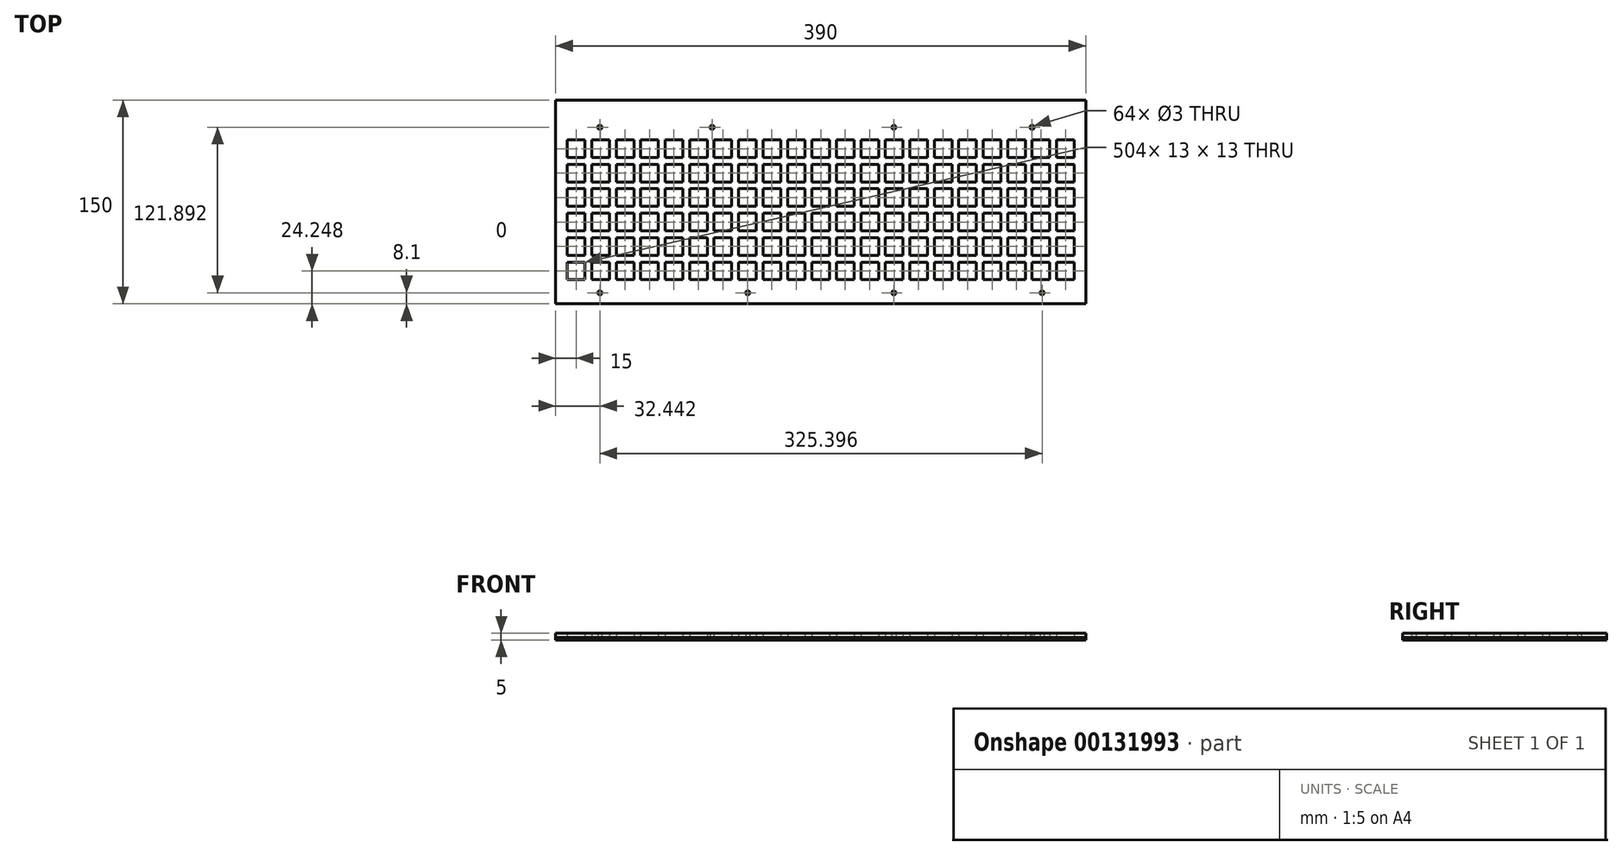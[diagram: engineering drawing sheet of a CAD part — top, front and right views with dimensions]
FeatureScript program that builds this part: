
annotation { "Feature Type Name" : "Feature", "Feature Type Description" : "" }
export const myFeature = defineFeature(function(context is Context, id is Id, definition is map)
    precondition{}
    {
        {
            var Q0;
            Q0=qCreatedBy(makeId("Top.planeOp"),FACE);
            var sketch = newSketch(context, id + "F0", { "sketchPlane" : qUnion([Q0])});
            skLineSegment(sketch, "E0.bottom", {"start": v(0, 0) * mm, "end": v(390, 0) * mm});
            skLineSegment(sketch, "E0.top", {"start": v(0, -150) * mm, "end": v(390, -150) * mm});
            skLineSegment(sketch, "E0.left", {"start": v(0, 0) * mm, "end": v(0, -150) * mm});
            skLineSegment(sketch, "E0.right", {"start": v(390, 0) * mm, "end": v(390, -150) * mm});
            skLineSegment(sketch, "E1.bottom", {"start": v(8.5, -29.25) * mm, "end": v(21.5, -29.25) * mm});
            skLineSegment(sketch, "E1.top", {"start": v(8.5, -42.25) * mm, "end": v(21.5, -42.25) * mm});
            skLineSegment(sketch, "E1.left", {"start": v(8.5, -29.25) * mm, "end": v(8.5, -42.25) * mm});
            skLineSegment(sketch, "E1.right", {"start": v(21.5, -29.25) * mm, "end": v(21.5, -42.25) * mm});
            skLineSegment(sketch, "E2.bottom", {"start": v(8.5, -47.25) * mm, "end": v(21.5, -47.25) * mm});
            skLineSegment(sketch, "E2.top", {"start": v(8.5, -60.25) * mm, "end": v(21.5, -60.25) * mm});
            skLineSegment(sketch, "E2.left", {"start": v(8.5, -47.25) * mm, "end": v(8.5, -60.25) * mm});
            skLineSegment(sketch, "E2.right", {"start": v(21.5, -47.25) * mm, "end": v(21.5, -60.25) * mm});
            skLineSegment(sketch, "E3.bottom", {"start": v(8.5, -65.25) * mm, "end": v(21.5, -65.25) * mm});
            skLineSegment(sketch, "E3.top", {"start": v(8.5, -78.25) * mm, "end": v(21.5, -78.25) * mm});
            skLineSegment(sketch, "E3.left", {"start": v(8.5, -65.25) * mm, "end": v(8.5, -78.25) * mm});
            skLineSegment(sketch, "E3.right", {"start": v(21.5, -65.25) * mm, "end": v(21.5, -78.25) * mm});
            skLineSegment(sketch, "E4.bottom", {"start": v(8.5, -83.25) * mm, "end": v(21.5, -83.25) * mm});
            skLineSegment(sketch, "E4.top", {"start": v(8.5, -96.25) * mm, "end": v(21.5, -96.25) * mm});
            skLineSegment(sketch, "E4.left", {"start": v(8.5, -83.25) * mm, "end": v(8.5, -96.25) * mm});
            skLineSegment(sketch, "E4.right", {"start": v(21.5, -83.25) * mm, "end": v(21.5, -96.25) * mm});
            skLineSegment(sketch, "E5.bottom", {"start": v(8.5, -101.25) * mm, "end": v(21.5, -101.25) * mm});
            skLineSegment(sketch, "E5.top", {"start": v(8.5, -114.25) * mm, "end": v(21.5, -114.25) * mm});
            skLineSegment(sketch, "E5.left", {"start": v(8.5, -101.25) * mm, "end": v(8.5, -114.25) * mm});
            skLineSegment(sketch, "E5.right", {"start": v(21.5, -101.25) * mm, "end": v(21.5, -114.25) * mm});
            skLineSegment(sketch, "E6.bottom", {"start": v(8.5, -119.25) * mm, "end": v(21.5, -119.25) * mm});
            skLineSegment(sketch, "E6.top", {"start": v(8.5, -132.25) * mm, "end": v(21.5, -132.25) * mm});
            skLineSegment(sketch, "E6.left", {"start": v(8.5, -119.25) * mm, "end": v(8.5, -132.25) * mm});
            skLineSegment(sketch, "E6.right", {"start": v(21.5, -119.25) * mm, "end": v(21.5, -132.25) * mm});
            skLineSegment(sketch, "E7", {"start": v(24, -21.56) * mm, "end": v(24, -144.75) * mm, "construction": true});
            skLineSegment(sketch, "E8.MirrorCS", {"start": v(39.5, -47.25) * mm, "end": v(39.5, -60.25) * mm});
            skLineSegment(sketch, "E9.MirrorCS", {"start": v(39.5, -60.25) * mm, "end": v(26.5, -60.25) * mm});
            skLineSegment(sketch, "E10.MirrorCS", {"start": v(39.5, -132.25) * mm, "end": v(26.5, -132.25) * mm});
            skLineSegment(sketch, "E11.MirrorCS", {"start": v(39.5, -119.25) * mm, "end": v(26.5, -119.25) * mm});
            skLineSegment(sketch, "E12.MirrorCS", {"start": v(39.5, -119.25) * mm, "end": v(39.5, -132.25) * mm});
            skLineSegment(sketch, "E13.MirrorCS", {"start": v(26.5, -29.25) * mm, "end": v(26.5, -42.25) * mm});
            skLineSegment(sketch, "E14.MirrorCS", {"start": v(39.5, -29.25) * mm, "end": v(26.5, -29.25) * mm});
            skLineSegment(sketch, "E15.MirrorCS", {"start": v(39.5, -101.25) * mm, "end": v(26.5, -101.25) * mm});
            skLineSegment(sketch, "E16.MirrorCS", {"start": v(26.5, -83.25) * mm, "end": v(26.5, -96.25) * mm});
            skLineSegment(sketch, "E17.MirrorCS", {"start": v(39.5, -83.25) * mm, "end": v(39.5, -96.25) * mm});
            skLineSegment(sketch, "E18.MirrorCS", {"start": v(39.5, -96.25) * mm, "end": v(26.5, -96.25) * mm});
            skLineSegment(sketch, "E19.MirrorCS", {"start": v(39.5, -83.25) * mm, "end": v(26.5, -83.25) * mm});
            skLineSegment(sketch, "E20.MirrorCS", {"start": v(26.5, -65.25) * mm, "end": v(26.5, -78.25) * mm});
            skLineSegment(sketch, "E21.MirrorCS", {"start": v(39.5, -65.25) * mm, "end": v(39.5, -78.25) * mm});
            skLineSegment(sketch, "E22.MirrorCS", {"start": v(39.5, -65.25) * mm, "end": v(26.5, -65.25) * mm});
            skLineSegment(sketch, "E23.MirrorCS", {"start": v(39.5, -78.25) * mm, "end": v(26.5, -78.25) * mm});
            skLineSegment(sketch, "E24.MirrorCS", {"start": v(26.5, -101.25) * mm, "end": v(26.5, -114.25) * mm});
            skLineSegment(sketch, "E25.MirrorCS", {"start": v(26.5, -47.25) * mm, "end": v(26.5, -60.25) * mm});
            skLineSegment(sketch, "E26.MirrorCS", {"start": v(26.5, -119.25) * mm, "end": v(26.5, -132.25) * mm});
            skLineSegment(sketch, "E27.MirrorCS", {"start": v(39.5, -101.25) * mm, "end": v(39.5, -114.25) * mm});
            skLineSegment(sketch, "E28.MirrorCS", {"start": v(39.5, -29.25) * mm, "end": v(39.5, -42.25) * mm});
            skLineSegment(sketch, "E29.MirrorCS", {"start": v(39.5, -114.25) * mm, "end": v(26.5, -114.25) * mm});
            skLineSegment(sketch, "E30.MirrorCS", {"start": v(39.5, -47.25) * mm, "end": v(26.5, -47.25) * mm});
            skLineSegment(sketch, "E31.MirrorCS", {"start": v(39.5, -42.25) * mm, "end": v(26.5, -42.25) * mm});
            skLineSegment(sketch, "E32", {"start": v(42, -21.56) * mm, "end": v(42, -144.75) * mm, "construction": true});
            skLineSegment(sketch, "E33.MirrorCS", {"start": v(57.5, -119.25) * mm, "end": v(57.5, -132.25) * mm});
            skLineSegment(sketch, "E34.MirrorCS", {"start": v(44.5, -29.25) * mm, "end": v(44.5, -42.25) * mm});
            skLineSegment(sketch, "E35.MirrorCS", {"start": v(44.5, -119.25) * mm, "end": v(44.5, -132.25) * mm});
            skLineSegment(sketch, "E36.MirrorCS", {"start": v(44.5, -114.25) * mm, "end": v(57.5, -114.25) * mm});
            skLineSegment(sketch, "E37.MirrorCS", {"start": v(75.5, -83.25) * mm, "end": v(75.5, -96.25) * mm});
            skLineSegment(sketch, "E38.MirrorCS", {"start": v(62.5, -65.25) * mm, "end": v(62.5, -78.25) * mm});
            skLineSegment(sketch, "E39.MirrorCS", {"start": v(75.5, -114.25) * mm, "end": v(62.5, -114.25) * mm});
            skLineSegment(sketch, "E40.MirrorCS", {"start": v(75.5, -42.25) * mm, "end": v(62.5, -42.25) * mm});
            skLineSegment(sketch, "E41.MirrorCS", {"start": v(57.5, -83.25) * mm, "end": v(57.5, -96.25) * mm});
            skLineSegment(sketch, "E42.MirrorCS", {"start": v(75.5, -101.25) * mm, "end": v(75.5, -114.25) * mm});
            skLineSegment(sketch, "E43.MirrorCS", {"start": v(75.5, -29.25) * mm, "end": v(75.5, -42.25) * mm});
            skLineSegment(sketch, "E44.MirrorCS", {"start": v(44.5, -83.25) * mm, "end": v(44.5, -96.25) * mm});
            skLineSegment(sketch, "E45.MirrorCS", {"start": v(44.5, -96.25) * mm, "end": v(57.5, -96.25) * mm});
            skLineSegment(sketch, "E46.MirrorCS", {"start": v(62.5, -101.25) * mm, "end": v(62.5, -114.25) * mm});
            skLineSegment(sketch, "E47.MirrorCS", {"start": v(62.5, -29.25) * mm, "end": v(62.5, -42.25) * mm});
            skLineSegment(sketch, "E48.MirrorCS", {"start": v(44.5, -83.25) * mm, "end": v(57.5, -83.25) * mm});
            skLineSegment(sketch, "E49.MirrorCS", {"start": v(75.5, -119.25) * mm, "end": v(62.5, -119.25) * mm});
            skLineSegment(sketch, "E50.MirrorCS", {"start": v(75.5, -47.25) * mm, "end": v(62.5, -47.25) * mm});
            skLineSegment(sketch, "E51.MirrorCS", {"start": v(57.5, -65.25) * mm, "end": v(57.5, -78.25) * mm});
            skLineSegment(sketch, "E52.MirrorCS", {"start": v(75.5, -60.25) * mm, "end": v(62.5, -60.25) * mm});
            skLineSegment(sketch, "E53.MirrorCS", {"start": v(75.5, -132.25) * mm, "end": v(62.5, -132.25) * mm});
            skLineSegment(sketch, "E54.MirrorCS", {"start": v(44.5, -132.25) * mm, "end": v(57.5, -132.25) * mm});
            skLineSegment(sketch, "E55.MirrorCS", {"start": v(75.5, -78.25) * mm, "end": v(62.5, -78.25) * mm});
            skLineSegment(sketch, "E56.MirrorCS", {"start": v(57.5, -101.25) * mm, "end": v(57.5, -114.25) * mm});
            skLineSegment(sketch, "E57.MirrorCS", {"start": v(44.5, -47.25) * mm, "end": v(44.5, -60.25) * mm});
            skLineSegment(sketch, "E58.MirrorCS", {"start": v(44.5, -65.25) * mm, "end": v(44.5, -78.25) * mm});
            skLineSegment(sketch, "E59.MirrorCS", {"start": v(75.5, -119.25) * mm, "end": v(75.5, -132.25) * mm});
            skLineSegment(sketch, "E60.MirrorCS", {"start": v(75.5, -47.25) * mm, "end": v(75.5, -60.25) * mm});
            skLineSegment(sketch, "E61.MirrorCS", {"start": v(75.5, -65.25) * mm, "end": v(75.5, -78.25) * mm});
            skLineSegment(sketch, "E62.MirrorCS", {"start": v(57.5, -47.25) * mm, "end": v(57.5, -60.25) * mm});
            skLineSegment(sketch, "E63.MirrorCS", {"start": v(44.5, -60.25) * mm, "end": v(57.5, -60.25) * mm});
            skLineSegment(sketch, "E64.MirrorCS", {"start": v(44.5, -65.25) * mm, "end": v(57.5, -65.25) * mm});
            skLineSegment(sketch, "E65.MirrorCS", {"start": v(62.5, -119.25) * mm, "end": v(62.5, -132.25) * mm});
            skLineSegment(sketch, "E66.MirrorCS", {"start": v(62.5, -47.25) * mm, "end": v(62.5, -60.25) * mm});
            skLineSegment(sketch, "E67.MirrorCS", {"start": v(44.5, -119.25) * mm, "end": v(57.5, -119.25) * mm});
            skLineSegment(sketch, "E68.MirrorCS", {"start": v(44.5, -101.25) * mm, "end": v(44.5, -114.25) * mm});
            skLineSegment(sketch, "E69.MirrorCS", {"start": v(75.5, -83.25) * mm, "end": v(62.5, -83.25) * mm});
            skLineSegment(sketch, "E70.MirrorCS", {"start": v(44.5, -101.25) * mm, "end": v(57.5, -101.25) * mm});
            skLineSegment(sketch, "E71.MirrorCS", {"start": v(75.5, -96.25) * mm, "end": v(62.5, -96.25) * mm});
            skLineSegment(sketch, "E72.MirrorCS", {"start": v(44.5, -78.25) * mm, "end": v(57.5, -78.25) * mm});
            skLineSegment(sketch, "E73.MirrorCS", {"start": v(75.5, -65.25) * mm, "end": v(62.5, -65.25) * mm});
            skLineSegment(sketch, "E74.MirrorCS", {"start": v(44.5, -42.25) * mm, "end": v(57.5, -42.25) * mm});
            skLineSegment(sketch, "E75.MirrorCS", {"start": v(44.5, -47.25) * mm, "end": v(57.5, -47.25) * mm});
            skLineSegment(sketch, "E76.MirrorCS", {"start": v(62.5, -83.25) * mm, "end": v(62.5, -96.25) * mm});
            skLineSegment(sketch, "E77.MirrorCS", {"start": v(75.5, -29.25) * mm, "end": v(62.5, -29.25) * mm});
            skLineSegment(sketch, "E78.MirrorCS", {"start": v(44.5, -29.25) * mm, "end": v(57.5, -29.25) * mm});
            skLineSegment(sketch, "E79.MirrorCS", {"start": v(75.5, -101.25) * mm, "end": v(62.5, -101.25) * mm});
            skLineSegment(sketch, "E80.MirrorCS", {"start": v(57.5, -29.25) * mm, "end": v(57.5, -42.25) * mm});
            skLineSegment(sketch, "E81", {"start": v(78, -21.56) * mm, "end": v(78, -144.75) * mm, "construction": true});
            skLineSegment(sketch, "E82.MirrorCS", {"start": v(111.5, -29.25) * mm, "end": v(111.5, -42.25) * mm});
            skLineSegment(sketch, "E83.MirrorCS", {"start": v(116.5, -83.25) * mm, "end": v(116.5, -96.25) * mm});
            skLineSegment(sketch, "E84.MirrorCS", {"start": v(93.5, -119.25) * mm, "end": v(93.5, -132.25) * mm});
            skLineSegment(sketch, "E85.MirrorCS", {"start": v(147.5, -47.25) * mm, "end": v(134.5, -47.25) * mm});
            skLineSegment(sketch, "E86.MirrorCS", {"start": v(147.5, -101.25) * mm, "end": v(134.5, -101.25) * mm});
            skLineSegment(sketch, "E87.MirrorCS", {"start": v(147.5, -29.25) * mm, "end": v(134.5, -29.25) * mm});
            skLineSegment(sketch, "E88.MirrorCS", {"start": v(147.5, -119.25) * mm, "end": v(134.5, -119.25) * mm});
            skLineSegment(sketch, "E89.MirrorCS", {"start": v(116.5, -83.25) * mm, "end": v(129.5, -83.25) * mm});
            skLineSegment(sketch, "E90.MirrorCS", {"start": v(111.5, -119.25) * mm, "end": v(111.5, -132.25) * mm});
            skLineSegment(sketch, "E91.MirrorCS", {"start": v(98.5, -29.25) * mm, "end": v(98.5, -42.25) * mm});
            skLineSegment(sketch, "E92.MirrorCS", {"start": v(129.5, -83.25) * mm, "end": v(129.5, -96.25) * mm});
            skLineSegment(sketch, "E93.MirrorCS", {"start": v(147.5, -65.25) * mm, "end": v(147.5, -78.25) * mm});
            skLineSegment(sketch, "E94.MirrorCS", {"start": v(116.5, -29.25) * mm, "end": v(129.5, -29.25) * mm});
            skLineSegment(sketch, "E95.MirrorCS", {"start": v(116.5, -47.25) * mm, "end": v(129.5, -47.25) * mm});
            skLineSegment(sketch, "E96.MirrorCS", {"start": v(93.5, -101.25) * mm, "end": v(93.5, -114.25) * mm});
            skLineSegment(sketch, "E97.MirrorCS", {"start": v(98.5, -47.25) * mm, "end": v(98.5, -60.25) * mm});
            skLineSegment(sketch, "E98.MirrorCS", {"start": v(93.5, -47.25) * mm, "end": v(93.5, -60.25) * mm});
            skLineSegment(sketch, "E99.MirrorCS", {"start": v(134.5, -83.25) * mm, "end": v(134.5, -96.25) * mm});
            skLineSegment(sketch, "E100.MirrorCS", {"start": v(111.5, -29.25) * mm, "end": v(98.5, -29.25) * mm});
            skLineSegment(sketch, "E101.MirrorCS", {"start": v(80.5, -29.25) * mm, "end": v(93.5, -29.25) * mm});
            skLineSegment(sketch, "E102.MirrorCS", {"start": v(129.5, -29.25) * mm, "end": v(129.5, -42.25) * mm});
            skLineSegment(sketch, "E103.MirrorCS", {"start": v(116.5, -114.25) * mm, "end": v(129.5, -114.25) * mm});
            skLineSegment(sketch, "E104.MirrorCS", {"start": v(111.5, -96.25) * mm, "end": v(98.5, -96.25) * mm});
            skLineSegment(sketch, "E105.MirrorCS", {"start": v(80.5, -65.25) * mm, "end": v(80.5, -78.25) * mm});
            skLineSegment(sketch, "E106.MirrorCS", {"start": v(93.5, -83.25) * mm, "end": v(93.5, -96.25) * mm});
            skLineSegment(sketch, "E107.MirrorCS", {"start": v(116.5, -119.25) * mm, "end": v(116.5, -132.25) * mm});
            skLineSegment(sketch, "E108.MirrorCS", {"start": v(116.5, -29.25) * mm, "end": v(116.5, -42.25) * mm});
            skLineSegment(sketch, "E109.MirrorCS", {"start": v(111.5, -83.25) * mm, "end": v(111.5, -96.25) * mm});
            skLineSegment(sketch, "E110.MirrorCS", {"start": v(80.5, -47.25) * mm, "end": v(80.5, -60.25) * mm});
            skLineSegment(sketch, "E111.MirrorCS", {"start": v(147.5, -96.25) * mm, "end": v(134.5, -96.25) * mm});
            skLineSegment(sketch, "E112.MirrorCS", {"start": v(134.5, -29.25) * mm, "end": v(134.5, -42.25) * mm});
            skLineSegment(sketch, "E113.MirrorCS", {"start": v(80.5, -132.25) * mm, "end": v(93.5, -132.25) * mm});
            skLineSegment(sketch, "E114.MirrorCS", {"start": v(80.5, -83.25) * mm, "end": v(93.5, -83.25) * mm});
            skLineSegment(sketch, "E115.MirrorCS", {"start": v(147.5, -47.25) * mm, "end": v(147.5, -60.25) * mm});
            skLineSegment(sketch, "E116.MirrorCS", {"start": v(147.5, -119.25) * mm, "end": v(147.5, -132.25) * mm});
            skLineSegment(sketch, "E117.MirrorCS", {"start": v(116.5, -65.25) * mm, "end": v(116.5, -78.25) * mm});
            skLineSegment(sketch, "E118.MirrorCS", {"start": v(80.5, -83.25) * mm, "end": v(80.5, -96.25) * mm});
            skLineSegment(sketch, "E119.MirrorCS", {"start": v(134.5, -101.25) * mm, "end": v(134.5, -114.25) * mm});
            skLineSegment(sketch, "E120.MirrorCS", {"start": v(111.5, -47.25) * mm, "end": v(98.5, -47.25) * mm});
            skLineSegment(sketch, "E121.MirrorCS", {"start": v(116.5, -101.25) * mm, "end": v(116.5, -114.25) * mm});
            skLineSegment(sketch, "E122.MirrorCS", {"start": v(116.5, -119.25) * mm, "end": v(129.5, -119.25) * mm});
            skLineSegment(sketch, "E123.MirrorCS", {"start": v(80.5, -29.25) * mm, "end": v(80.5, -42.25) * mm});
            skLineSegment(sketch, "E124.MirrorCS", {"start": v(80.5, -119.25) * mm, "end": v(80.5, -132.25) * mm});
            skLineSegment(sketch, "E125.MirrorCS", {"start": v(147.5, -83.25) * mm, "end": v(134.5, -83.25) * mm});
            skLineSegment(sketch, "E126.MirrorCS", {"start": v(111.5, -42.25) * mm, "end": v(98.5, -42.25) * mm});
            skLineSegment(sketch, "E127.MirrorCS", {"start": v(116.5, -132.25) * mm, "end": v(129.5, -132.25) * mm});
            skLineSegment(sketch, "E128.MirrorCS", {"start": v(129.5, -119.25) * mm, "end": v(129.5, -132.25) * mm});
            skLineSegment(sketch, "E129.MirrorCS", {"start": v(80.5, -101.25) * mm, "end": v(80.5, -114.25) * mm});
            skLineSegment(sketch, "E130.MirrorCS", {"start": v(111.5, -65.25) * mm, "end": v(111.5, -78.25) * mm});
            skLineSegment(sketch, "E131.MirrorCS", {"start": v(80.5, -60.25) * mm, "end": v(93.5, -60.25) * mm});
            skLineSegment(sketch, "E132.MirrorCS", {"start": v(111.5, -101.25) * mm, "end": v(111.5, -114.25) * mm});
            skLineSegment(sketch, "E133.MirrorCS", {"start": v(134.5, -65.25) * mm, "end": v(134.5, -78.25) * mm});
            skLineSegment(sketch, "E134.MirrorCS", {"start": v(147.5, -60.25) * mm, "end": v(134.5, -60.25) * mm});
            skLineSegment(sketch, "E135.MirrorCS", {"start": v(147.5, -132.25) * mm, "end": v(134.5, -132.25) * mm});
            skLineSegment(sketch, "E136.MirrorCS", {"start": v(129.5, -65.25) * mm, "end": v(129.5, -78.25) * mm});
            skLineSegment(sketch, "E137.MirrorCS", {"start": v(111.5, -114.25) * mm, "end": v(98.5, -114.25) * mm});
            skLineSegment(sketch, "E138.MirrorCS", {"start": v(80.5, -65.25) * mm, "end": v(93.5, -65.25) * mm});
            skLineSegment(sketch, "E139.MirrorCS", {"start": v(116.5, -60.25) * mm, "end": v(129.5, -60.25) * mm});
            skLineSegment(sketch, "E140.MirrorCS", {"start": v(129.5, -47.25) * mm, "end": v(129.5, -60.25) * mm});
            skLineSegment(sketch, "E141.MirrorCS", {"start": v(98.5, -83.25) * mm, "end": v(98.5, -96.25) * mm});
            skLineSegment(sketch, "E142.MirrorCS", {"start": v(111.5, -47.25) * mm, "end": v(111.5, -60.25) * mm});
            skLineSegment(sketch, "E143.MirrorCS", {"start": v(80.5, -47.25) * mm, "end": v(93.5, -47.25) * mm});
            skLineSegment(sketch, "E144.MirrorCS", {"start": v(116.5, -96.25) * mm, "end": v(129.5, -96.25) * mm});
            skLineSegment(sketch, "E145.MirrorCS", {"start": v(111.5, -119.25) * mm, "end": v(98.5, -119.25) * mm});
            skLineSegment(sketch, "E146.MirrorCS", {"start": v(98.5, -65.25) * mm, "end": v(98.5, -78.25) * mm});
            skLineSegment(sketch, "E147.MirrorCS", {"start": v(111.5, -60.25) * mm, "end": v(98.5, -60.25) * mm});
            skLineSegment(sketch, "E148.MirrorCS", {"start": v(147.5, -83.25) * mm, "end": v(147.5, -96.25) * mm});
            skLineSegment(sketch, "E149.MirrorCS", {"start": v(111.5, -65.25) * mm, "end": v(98.5, -65.25) * mm});
            skLineSegment(sketch, "E150.MirrorCS", {"start": v(111.5, -83.25) * mm, "end": v(98.5, -83.25) * mm});
            skLineSegment(sketch, "E151.MirrorCS", {"start": v(116.5, -42.25) * mm, "end": v(129.5, -42.25) * mm});
            skLineSegment(sketch, "E152.MirrorCS", {"start": v(147.5, -42.25) * mm, "end": v(134.5, -42.25) * mm});
            skLineSegment(sketch, "E153.MirrorCS", {"start": v(147.5, -114.25) * mm, "end": v(134.5, -114.25) * mm});
            skLineSegment(sketch, "E154.MirrorCS", {"start": v(98.5, -101.25) * mm, "end": v(98.5, -114.25) * mm});
            skLineSegment(sketch, "E155.MirrorCS", {"start": v(80.5, -42.25) * mm, "end": v(93.5, -42.25) * mm});
            skLineSegment(sketch, "E156.MirrorCS", {"start": v(129.5, -101.25) * mm, "end": v(129.5, -114.25) * mm});
            skLineSegment(sketch, "E157.MirrorCS", {"start": v(116.5, -47.25) * mm, "end": v(116.5, -60.25) * mm});
            skLineSegment(sketch, "E158.MirrorCS", {"start": v(111.5, -78.25) * mm, "end": v(98.5, -78.25) * mm});
            skLineSegment(sketch, "E159.MirrorCS", {"start": v(147.5, -101.25) * mm, "end": v(147.5, -114.25) * mm});
            skLineSegment(sketch, "E160.MirrorCS", {"start": v(93.5, -29.25) * mm, "end": v(93.5, -42.25) * mm});
            skLineSegment(sketch, "E161.MirrorCS", {"start": v(116.5, -101.25) * mm, "end": v(129.5, -101.25) * mm});
            skLineSegment(sketch, "E162.MirrorCS", {"start": v(80.5, -101.25) * mm, "end": v(93.5, -101.25) * mm});
            skLineSegment(sketch, "E163.MirrorCS", {"start": v(147.5, -29.25) * mm, "end": v(147.5, -42.25) * mm});
            skLineSegment(sketch, "E164.MirrorCS", {"start": v(80.5, -119.25) * mm, "end": v(93.5, -119.25) * mm});
            skLineSegment(sketch, "E165.MirrorCS", {"start": v(98.5, -119.25) * mm, "end": v(98.5, -132.25) * mm});
            skLineSegment(sketch, "E166.MirrorCS", {"start": v(147.5, -78.25) * mm, "end": v(134.5, -78.25) * mm});
            skLineSegment(sketch, "E167.MirrorCS", {"start": v(147.5, -65.25) * mm, "end": v(134.5, -65.25) * mm});
            skLineSegment(sketch, "E168.MirrorCS", {"start": v(80.5, -78.25) * mm, "end": v(93.5, -78.25) * mm});
            skLineSegment(sketch, "E169.MirrorCS", {"start": v(80.5, -96.25) * mm, "end": v(93.5, -96.25) * mm});
            skLineSegment(sketch, "E170.MirrorCS", {"start": v(116.5, -78.25) * mm, "end": v(129.5, -78.25) * mm});
            skLineSegment(sketch, "E171.MirrorCS", {"start": v(80.5, -114.25) * mm, "end": v(93.5, -114.25) * mm});
            skLineSegment(sketch, "E172.MirrorCS", {"start": v(134.5, -119.25) * mm, "end": v(134.5, -132.25) * mm});
            skLineSegment(sketch, "E173.MirrorCS", {"start": v(116.5, -65.25) * mm, "end": v(129.5, -65.25) * mm});
            skLineSegment(sketch, "E174.MirrorCS", {"start": v(93.5, -65.25) * mm, "end": v(93.5, -78.25) * mm});
            skLineSegment(sketch, "E175.MirrorCS", {"start": v(134.5, -47.25) * mm, "end": v(134.5, -60.25) * mm});
            skLineSegment(sketch, "E176.MirrorCS", {"start": v(111.5, -101.25) * mm, "end": v(98.5, -101.25) * mm});
            skLineSegment(sketch, "E177.MirrorCS", {"start": v(111.5, -132.25) * mm, "end": v(98.5, -132.25) * mm});
            skLineSegment(sketch, "E178", {"start": v(150, -21.56) * mm, "end": v(150, -144.75) * mm, "construction": true});
            skLineSegment(sketch, "E179.MirrorCS", {"start": v(291.5, -83.25) * mm, "end": v(291.5, -96.25) * mm});
            skLineSegment(sketch, "E180.MirrorCS", {"start": v(291.5, -101.25) * mm, "end": v(278.5, -101.25) * mm});
            skLineSegment(sketch, "E181.MirrorCS", {"start": v(291.5, -29.25) * mm, "end": v(278.5, -29.25) * mm});
            skLineSegment(sketch, "E182.MirrorCS", {"start": v(291.5, -29.25) * mm, "end": v(291.5, -42.25) * mm});
            skLineSegment(sketch, "E183.MirrorCS", {"start": v(291.5, -47.25) * mm, "end": v(291.5, -60.25) * mm});
            skLineSegment(sketch, "E184.MirrorCS", {"start": v(291.5, -119.25) * mm, "end": v(291.5, -132.25) * mm});
            skLineSegment(sketch, "E185.MirrorCS", {"start": v(291.5, -65.25) * mm, "end": v(278.5, -65.25) * mm});
            skLineSegment(sketch, "E186.MirrorCS", {"start": v(291.5, -65.25) * mm, "end": v(291.5, -78.25) * mm});
            skLineSegment(sketch, "E187.MirrorCS", {"start": v(260.5, -119.25) * mm, "end": v(260.5, -132.25) * mm});
            skLineSegment(sketch, "E188.MirrorCS", {"start": v(255.5, -83.25) * mm, "end": v(255.5, -96.25) * mm});
            skLineSegment(sketch, "E189.MirrorCS", {"start": v(170.5, -101.25) * mm, "end": v(170.5, -114.25) * mm});
            skLineSegment(sketch, "E190.MirrorCS", {"start": v(224.5, -65.25) * mm, "end": v(224.5, -78.25) * mm});
            skLineSegment(sketch, "E191.MirrorCS", {"start": v(255.5, -96.25) * mm, "end": v(242.5, -96.25) * mm});
            skLineSegment(sketch, "E192.MirrorCS", {"start": v(260.5, -114.25) * mm, "end": v(273.5, -114.25) * mm});
            skLineSegment(sketch, "E193.MirrorCS", {"start": v(273.5, -29.25) * mm, "end": v(273.5, -42.25) * mm});
            skLineSegment(sketch, "E194.MirrorCS", {"start": v(152.5, -83.25) * mm, "end": v(165.5, -83.25) * mm});
            skLineSegment(sketch, "E195.MirrorCS", {"start": v(152.5, -65.25) * mm, "end": v(152.5, -78.25) * mm});
            skLineSegment(sketch, "E196.MirrorCS", {"start": v(224.5, -29.25) * mm, "end": v(237.5, -29.25) * mm});
            skLineSegment(sketch, "E197.MirrorCS", {"start": v(183.5, -47.25) * mm, "end": v(183.5, -60.25) * mm});
            skLineSegment(sketch, "E198.MirrorCS", {"start": v(152.5, -101.25) * mm, "end": v(152.5, -114.25) * mm});
            skLineSegment(sketch, "E199.MirrorCS", {"start": v(219.5, -47.25) * mm, "end": v(206.5, -47.25) * mm});
            skLineSegment(sketch, "E200.MirrorCS", {"start": v(219.5, -119.25) * mm, "end": v(219.5, -132.25) * mm});
            skLineSegment(sketch, "E201.MirrorCS", {"start": v(237.5, -29.25) * mm, "end": v(237.5, -42.25) * mm});
            skLineSegment(sketch, "E202.MirrorCS", {"start": v(260.5, -42.25) * mm, "end": v(273.5, -42.25) * mm});
            skLineSegment(sketch, "E203.MirrorCS", {"start": v(260.5, -101.25) * mm, "end": v(273.5, -101.25) * mm});
            skLineSegment(sketch, "E204.MirrorCS", {"start": v(183.5, -132.25) * mm, "end": v(170.5, -132.25) * mm});
            skLineSegment(sketch, "E205.MirrorCS", {"start": v(152.5, -96.25) * mm, "end": v(165.5, -96.25) * mm});
            skLineSegment(sketch, "E206.MirrorCS", {"start": v(183.5, -47.25) * mm, "end": v(170.5, -47.25) * mm});
            skLineSegment(sketch, "E207.MirrorCS", {"start": v(224.5, -101.25) * mm, "end": v(237.5, -101.25) * mm});
            skLineSegment(sketch, "E208.MirrorCS", {"start": v(291.5, -114.25) * mm, "end": v(278.5, -114.25) * mm});
            skLineSegment(sketch, "E209.MirrorCS", {"start": v(291.5, -42.25) * mm, "end": v(278.5, -42.25) * mm});
            skLineSegment(sketch, "E210.MirrorCS", {"start": v(255.5, -65.25) * mm, "end": v(242.5, -65.25) * mm});
            skLineSegment(sketch, "E211.MirrorCS", {"start": v(255.5, -83.25) * mm, "end": v(242.5, -83.25) * mm});
            skLineSegment(sketch, "E212.MirrorCS", {"start": v(273.5, -83.25) * mm, "end": v(273.5, -96.25) * mm});
            skLineSegment(sketch, "E213.MirrorCS", {"start": v(165.5, -29.25) * mm, "end": v(165.5, -42.25) * mm});
            skLineSegment(sketch, "E214.MirrorCS", {"start": v(242.5, -29.25) * mm, "end": v(242.5, -42.25) * mm});
            skLineSegment(sketch, "E215.MirrorCS", {"start": v(206.5, -101.25) * mm, "end": v(206.5, -114.25) * mm});
            skLineSegment(sketch, "E216.MirrorCS", {"start": v(188.5, -101.25) * mm, "end": v(201.5, -101.25) * mm});
            skLineSegment(sketch, "E217.MirrorCS", {"start": v(206.5, -29.25) * mm, "end": v(206.5, -42.25) * mm});
            skLineSegment(sketch, "E218.MirrorCS", {"start": v(183.5, -96.25) * mm, "end": v(170.5, -96.25) * mm});
            skLineSegment(sketch, "E219.MirrorCS", {"start": v(291.5, -101.25) * mm, "end": v(291.5, -114.25) * mm});
            skLineSegment(sketch, "E220.MirrorCS", {"start": v(237.5, -119.25) * mm, "end": v(237.5, -132.25) * mm});
            skLineSegment(sketch, "E221.MirrorCS", {"start": v(224.5, -119.25) * mm, "end": v(237.5, -119.25) * mm});
            skLineSegment(sketch, "E222.MirrorCS", {"start": v(242.5, -119.25) * mm, "end": v(242.5, -132.25) * mm});
            skLineSegment(sketch, "E223.MirrorCS", {"start": v(260.5, -83.25) * mm, "end": v(260.5, -96.25) * mm});
            skLineSegment(sketch, "E224.MirrorCS", {"start": v(219.5, -101.25) * mm, "end": v(219.5, -114.25) * mm});
            skLineSegment(sketch, "E225.MirrorCS", {"start": v(219.5, -132.25) * mm, "end": v(206.5, -132.25) * mm});
            skLineSegment(sketch, "E226.MirrorCS", {"start": v(201.5, -47.25) * mm, "end": v(201.5, -60.25) * mm});
            skLineSegment(sketch, "E227.MirrorCS", {"start": v(188.5, -132.25) * mm, "end": v(201.5, -132.25) * mm});
            skLineSegment(sketch, "E228.MirrorCS", {"start": v(183.5, -101.25) * mm, "end": v(170.5, -101.25) * mm});
            skLineSegment(sketch, "E229.MirrorCS", {"start": v(188.5, -119.25) * mm, "end": v(201.5, -119.25) * mm});
            skLineSegment(sketch, "E230.MirrorCS", {"start": v(278.5, -65.25) * mm, "end": v(278.5, -78.25) * mm});
            skLineSegment(sketch, "E231.MirrorCS", {"start": v(255.5, -65.25) * mm, "end": v(255.5, -78.25) * mm});
            skLineSegment(sketch, "E232.MirrorCS", {"start": v(224.5, -101.25) * mm, "end": v(224.5, -114.25) * mm});
            skLineSegment(sketch, "E233.MirrorCS", {"start": v(273.5, -119.25) * mm, "end": v(273.5, -132.25) * mm});
            skLineSegment(sketch, "E234.MirrorCS", {"start": v(260.5, -132.25) * mm, "end": v(273.5, -132.25) * mm});
            skLineSegment(sketch, "E235.MirrorCS", {"start": v(206.5, -83.25) * mm, "end": v(206.5, -96.25) * mm});
            skLineSegment(sketch, "E236.MirrorCS", {"start": v(183.5, -119.25) * mm, "end": v(170.5, -119.25) * mm});
            skLineSegment(sketch, "E237.MirrorCS", {"start": v(170.5, -83.25) * mm, "end": v(170.5, -96.25) * mm});
            skLineSegment(sketch, "E238.MirrorCS", {"start": v(188.5, -119.25) * mm, "end": v(188.5, -132.25) * mm});
            skLineSegment(sketch, "E239.MirrorCS", {"start": v(183.5, -78.25) * mm, "end": v(170.5, -78.25) * mm});
            skLineSegment(sketch, "E240.MirrorCS", {"start": v(255.5, -42.25) * mm, "end": v(242.5, -42.25) * mm});
            skLineSegment(sketch, "E241.MirrorCS", {"start": v(201.5, -101.25) * mm, "end": v(201.5, -114.25) * mm});
            skLineSegment(sketch, "E242.MirrorCS", {"start": v(219.5, -65.25) * mm, "end": v(206.5, -65.25) * mm});
            skLineSegment(sketch, "E243.MirrorCS", {"start": v(255.5, -29.25) * mm, "end": v(255.5, -42.25) * mm});
            skLineSegment(sketch, "E244.MirrorCS", {"start": v(260.5, -96.25) * mm, "end": v(273.5, -96.25) * mm});
            skLineSegment(sketch, "E245.MirrorCS", {"start": v(291.5, -83.25) * mm, "end": v(278.5, -83.25) * mm});
            skLineSegment(sketch, "E246.MirrorCS", {"start": v(278.5, -29.25) * mm, "end": v(278.5, -42.25) * mm});
            skLineSegment(sketch, "E247.MirrorCS", {"start": v(278.5, -101.25) * mm, "end": v(278.5, -114.25) * mm});
            skLineSegment(sketch, "E248.MirrorCS", {"start": v(224.5, -119.25) * mm, "end": v(224.5, -132.25) * mm});
            skLineSegment(sketch, "E249.MirrorCS", {"start": v(224.5, -29.25) * mm, "end": v(224.5, -42.25) * mm});
            skLineSegment(sketch, "E250.MirrorCS", {"start": v(260.5, -101.25) * mm, "end": v(260.5, -114.25) * mm});
            skLineSegment(sketch, "E251.MirrorCS", {"start": v(260.5, -119.25) * mm, "end": v(273.5, -119.25) * mm});
            skLineSegment(sketch, "E252.MirrorCS", {"start": v(219.5, -29.25) * mm, "end": v(219.5, -42.25) * mm});
            skLineSegment(sketch, "E253.MirrorCS", {"start": v(206.5, -47.25) * mm, "end": v(206.5, -60.25) * mm});
            skLineSegment(sketch, "E254.MirrorCS", {"start": v(188.5, -29.25) * mm, "end": v(188.5, -42.25) * mm});
            skLineSegment(sketch, "E255.MirrorCS", {"start": v(237.5, -47.25) * mm, "end": v(237.5, -60.25) * mm});
            skLineSegment(sketch, "E256.MirrorCS", {"start": v(224.5, -47.25) * mm, "end": v(237.5, -47.25) * mm});
            skLineSegment(sketch, "E257.MirrorCS", {"start": v(201.5, -65.25) * mm, "end": v(201.5, -78.25) * mm});
            skLineSegment(sketch, "E258.MirrorCS", {"start": v(219.5, -101.25) * mm, "end": v(206.5, -101.25) * mm});
            skLineSegment(sketch, "E259.MirrorCS", {"start": v(188.5, -65.25) * mm, "end": v(188.5, -78.25) * mm});
            skLineSegment(sketch, "E260.MirrorCS", {"start": v(219.5, -83.25) * mm, "end": v(206.5, -83.25) * mm});
            skLineSegment(sketch, "E261.MirrorCS", {"start": v(183.5, -119.25) * mm, "end": v(183.5, -132.25) * mm});
            skLineSegment(sketch, "E262.MirrorCS", {"start": v(201.5, -29.25) * mm, "end": v(201.5, -42.25) * mm});
            skLineSegment(sketch, "E263.MirrorCS", {"start": v(255.5, -47.25) * mm, "end": v(242.5, -47.25) * mm});
            skLineSegment(sketch, "E264.MirrorCS", {"start": v(219.5, -114.25) * mm, "end": v(206.5, -114.25) * mm});
            skLineSegment(sketch, "E265.MirrorCS", {"start": v(219.5, -42.25) * mm, "end": v(206.5, -42.25) * mm});
            skLineSegment(sketch, "E266.MirrorCS", {"start": v(183.5, -60.25) * mm, "end": v(170.5, -60.25) * mm});
            skLineSegment(sketch, "E267.MirrorCS", {"start": v(170.5, -47.25) * mm, "end": v(170.5, -60.25) * mm});
            skLineSegment(sketch, "E268.MirrorCS", {"start": v(224.5, -47.25) * mm, "end": v(224.5, -60.25) * mm});
            skLineSegment(sketch, "E269.MirrorCS", {"start": v(291.5, -96.25) * mm, "end": v(278.5, -96.25) * mm});
            skLineSegment(sketch, "E270.MirrorCS", {"start": v(219.5, -83.25) * mm, "end": v(219.5, -96.25) * mm});
            skLineSegment(sketch, "E271.MirrorCS", {"start": v(152.5, -60.25) * mm, "end": v(165.5, -60.25) * mm});
            skLineSegment(sketch, "E272.MirrorCS", {"start": v(152.5, -78.25) * mm, "end": v(165.5, -78.25) * mm});
            skLineSegment(sketch, "E273.MirrorCS", {"start": v(188.5, -83.25) * mm, "end": v(201.5, -83.25) * mm});
            skLineSegment(sketch, "E274.MirrorCS", {"start": v(255.5, -101.25) * mm, "end": v(242.5, -101.25) * mm});
            skLineSegment(sketch, "E275.MirrorCS", {"start": v(255.5, -132.25) * mm, "end": v(242.5, -132.25) * mm});
            skLineSegment(sketch, "E276.MirrorCS", {"start": v(152.5, -132.25) * mm, "end": v(165.5, -132.25) * mm});
            skLineSegment(sketch, "E277.MirrorCS", {"start": v(152.5, -101.25) * mm, "end": v(165.5, -101.25) * mm});
            skLineSegment(sketch, "E278.MirrorCS", {"start": v(165.5, -101.25) * mm, "end": v(165.5, -114.25) * mm});
            skLineSegment(sketch, "E279.MirrorCS", {"start": v(170.5, -29.25) * mm, "end": v(170.5, -42.25) * mm});
            skLineSegment(sketch, "E280.MirrorCS", {"start": v(278.5, -47.25) * mm, "end": v(278.5, -60.25) * mm});
            skLineSegment(sketch, "E281.MirrorCS", {"start": v(278.5, -119.25) * mm, "end": v(278.5, -132.25) * mm});
            skLineSegment(sketch, "E282.MirrorCS", {"start": v(260.5, -65.25) * mm, "end": v(273.5, -65.25) * mm});
            skLineSegment(sketch, "E283.MirrorCS", {"start": v(237.5, -65.25) * mm, "end": v(237.5, -78.25) * mm});
            skLineSegment(sketch, "E284.MirrorCS", {"start": v(183.5, -42.25) * mm, "end": v(170.5, -42.25) * mm});
            skLineSegment(sketch, "E285.MirrorCS", {"start": v(165.5, -65.25) * mm, "end": v(165.5, -78.25) * mm});
            skLineSegment(sketch, "E286.MirrorCS", {"start": v(183.5, -65.25) * mm, "end": v(183.5, -78.25) * mm});
            skLineSegment(sketch, "E287.MirrorCS", {"start": v(188.5, -65.25) * mm, "end": v(201.5, -65.25) * mm});
            skLineSegment(sketch, "E288.MirrorCS", {"start": v(201.5, -119.25) * mm, "end": v(201.5, -132.25) * mm});
            skLineSegment(sketch, "E289.MirrorCS", {"start": v(152.5, -65.25) * mm, "end": v(165.5, -65.25) * mm});
            skLineSegment(sketch, "E290.MirrorCS", {"start": v(224.5, -132.25) * mm, "end": v(237.5, -132.25) * mm});
            skLineSegment(sketch, "E291.MirrorCS", {"start": v(224.5, -83.25) * mm, "end": v(237.5, -83.25) * mm});
            skLineSegment(sketch, "E292.MirrorCS", {"start": v(152.5, -47.25) * mm, "end": v(165.5, -47.25) * mm});
            skLineSegment(sketch, "E293.MirrorCS", {"start": v(219.5, -29.25) * mm, "end": v(206.5, -29.25) * mm});
            skLineSegment(sketch, "E294.MirrorCS", {"start": v(260.5, -65.25) * mm, "end": v(260.5, -78.25) * mm});
            skLineSegment(sketch, "E295.MirrorCS", {"start": v(224.5, -83.25) * mm, "end": v(224.5, -96.25) * mm});
            skLineSegment(sketch, "E296.MirrorCS", {"start": v(260.5, -29.25) * mm, "end": v(260.5, -42.25) * mm});
            skLineSegment(sketch, "E297.MirrorCS", {"start": v(188.5, -101.25) * mm, "end": v(188.5, -114.25) * mm});
            skLineSegment(sketch, "E298.MirrorCS", {"start": v(152.5, -119.25) * mm, "end": v(152.5, -132.25) * mm});
            skLineSegment(sketch, "E299.MirrorCS", {"start": v(219.5, -119.25) * mm, "end": v(206.5, -119.25) * mm});
            skLineSegment(sketch, "E300.MirrorCS", {"start": v(152.5, -83.25) * mm, "end": v(152.5, -96.25) * mm});
            skLineSegment(sketch, "E301.MirrorCS", {"start": v(255.5, -101.25) * mm, "end": v(255.5, -114.25) * mm});
            skLineSegment(sketch, "E302.MirrorCS", {"start": v(224.5, -60.25) * mm, "end": v(237.5, -60.25) * mm});
            skLineSegment(sketch, "E303.MirrorCS", {"start": v(188.5, -29.25) * mm, "end": v(201.5, -29.25) * mm});
            skLineSegment(sketch, "E304.MirrorCS", {"start": v(206.5, -119.25) * mm, "end": v(206.5, -132.25) * mm});
            skLineSegment(sketch, "E305.MirrorCS", {"start": v(188.5, -47.25) * mm, "end": v(188.5, -60.25) * mm});
            skLineSegment(sketch, "E306.MirrorCS", {"start": v(188.5, -78.25) * mm, "end": v(201.5, -78.25) * mm});
            skLineSegment(sketch, "E307.MirrorCS", {"start": v(255.5, -29.25) * mm, "end": v(242.5, -29.25) * mm});
            skLineSegment(sketch, "E308.MirrorCS", {"start": v(188.5, -42.25) * mm, "end": v(201.5, -42.25) * mm});
            skLineSegment(sketch, "E309.MirrorCS", {"start": v(206.5, -65.25) * mm, "end": v(206.5, -78.25) * mm});
            skLineSegment(sketch, "E310.MirrorCS", {"start": v(170.5, -119.25) * mm, "end": v(170.5, -132.25) * mm});
            skLineSegment(sketch, "E311.MirrorCS", {"start": v(255.5, -60.25) * mm, "end": v(242.5, -60.25) * mm});
            skLineSegment(sketch, "E312.MirrorCS", {"start": v(165.5, -47.25) * mm, "end": v(165.5, -60.25) * mm});
            skLineSegment(sketch, "E313.MirrorCS", {"start": v(183.5, -29.25) * mm, "end": v(170.5, -29.25) * mm});
            skLineSegment(sketch, "E314.MirrorCS", {"start": v(219.5, -47.25) * mm, "end": v(219.5, -60.25) * mm});
            skLineSegment(sketch, "E315.MirrorCS", {"start": v(183.5, -29.25) * mm, "end": v(183.5, -42.25) * mm});
            skLineSegment(sketch, "E316.MirrorCS", {"start": v(188.5, -60.25) * mm, "end": v(201.5, -60.25) * mm});
            skLineSegment(sketch, "E317.MirrorCS", {"start": v(152.5, -29.25) * mm, "end": v(152.5, -42.25) * mm});
            skLineSegment(sketch, "E318.MirrorCS", {"start": v(242.5, -65.25) * mm, "end": v(242.5, -78.25) * mm});
            skLineSegment(sketch, "E319.MirrorCS", {"start": v(255.5, -119.25) * mm, "end": v(242.5, -119.25) * mm});
            skLineSegment(sketch, "E320.MirrorCS", {"start": v(183.5, -83.25) * mm, "end": v(183.5, -96.25) * mm});
            skLineSegment(sketch, "E321.MirrorCS", {"start": v(291.5, -47.25) * mm, "end": v(278.5, -47.25) * mm});
            skLineSegment(sketch, "E322.MirrorCS", {"start": v(165.5, -83.25) * mm, "end": v(165.5, -96.25) * mm});
            skLineSegment(sketch, "E323.MirrorCS", {"start": v(291.5, -119.25) * mm, "end": v(278.5, -119.25) * mm});
            skLineSegment(sketch, "E324.MirrorCS", {"start": v(260.5, -83.25) * mm, "end": v(273.5, -83.25) * mm});
            skLineSegment(sketch, "E325.MirrorCS", {"start": v(255.5, -119.25) * mm, "end": v(255.5, -132.25) * mm});
            skLineSegment(sketch, "E326.MirrorCS", {"start": v(260.5, -47.25) * mm, "end": v(273.5, -47.25) * mm});
            skLineSegment(sketch, "E327.MirrorCS", {"start": v(224.5, -96.25) * mm, "end": v(237.5, -96.25) * mm});
            skLineSegment(sketch, "E328.MirrorCS", {"start": v(260.5, -29.25) * mm, "end": v(273.5, -29.25) * mm});
            skLineSegment(sketch, "E329.MirrorCS", {"start": v(224.5, -78.25) * mm, "end": v(237.5, -78.25) * mm});
            skLineSegment(sketch, "E330.MirrorCS", {"start": v(201.5, -83.25) * mm, "end": v(201.5, -96.25) * mm});
            skLineSegment(sketch, "E331.MirrorCS", {"start": v(183.5, -65.25) * mm, "end": v(170.5, -65.25) * mm});
            skLineSegment(sketch, "E332.MirrorCS", {"start": v(152.5, -47.25) * mm, "end": v(152.5, -60.25) * mm});
            skLineSegment(sketch, "E333.MirrorCS", {"start": v(219.5, -60.25) * mm, "end": v(206.5, -60.25) * mm});
            skLineSegment(sketch, "E334.MirrorCS", {"start": v(237.5, -83.25) * mm, "end": v(237.5, -96.25) * mm});
            skLineSegment(sketch, "E335.MirrorCS", {"start": v(188.5, -83.25) * mm, "end": v(188.5, -96.25) * mm});
            skLineSegment(sketch, "E336.MirrorCS", {"start": v(237.5, -101.25) * mm, "end": v(237.5, -114.25) * mm});
            skLineSegment(sketch, "E337.MirrorCS", {"start": v(278.5, -83.25) * mm, "end": v(278.5, -96.25) * mm});
            skLineSegment(sketch, "E338.MirrorCS", {"start": v(219.5, -78.25) * mm, "end": v(206.5, -78.25) * mm});
            skLineSegment(sketch, "E339.MirrorCS", {"start": v(152.5, -42.25) * mm, "end": v(165.5, -42.25) * mm});
            skLineSegment(sketch, "E340.MirrorCS", {"start": v(170.5, -65.25) * mm, "end": v(170.5, -78.25) * mm});
            skLineSegment(sketch, "E341.MirrorCS", {"start": v(255.5, -78.25) * mm, "end": v(242.5, -78.25) * mm});
            skLineSegment(sketch, "E342.MirrorCS", {"start": v(255.5, -114.25) * mm, "end": v(242.5, -114.25) * mm});
            skLineSegment(sketch, "E343.MirrorCS", {"start": v(273.5, -65.25) * mm, "end": v(273.5, -78.25) * mm});
            skLineSegment(sketch, "E344.MirrorCS", {"start": v(291.5, -132.25) * mm, "end": v(278.5, -132.25) * mm});
            skLineSegment(sketch, "E345.MirrorCS", {"start": v(291.5, -60.25) * mm, "end": v(278.5, -60.25) * mm});
            skLineSegment(sketch, "E346.MirrorCS", {"start": v(152.5, -119.25) * mm, "end": v(165.5, -119.25) * mm});
            skLineSegment(sketch, "E347.MirrorCS", {"start": v(188.5, -96.25) * mm, "end": v(201.5, -96.25) * mm});
            skLineSegment(sketch, "E348.MirrorCS", {"start": v(242.5, -47.25) * mm, "end": v(242.5, -60.25) * mm});
            skLineSegment(sketch, "E349.MirrorCS", {"start": v(165.5, -119.25) * mm, "end": v(165.5, -132.25) * mm});
            skLineSegment(sketch, "E350.MirrorCS", {"start": v(188.5, -47.25) * mm, "end": v(201.5, -47.25) * mm});
            skLineSegment(sketch, "E351.MirrorCS", {"start": v(260.5, -47.25) * mm, "end": v(260.5, -60.25) * mm});
            skLineSegment(sketch, "E352.MirrorCS", {"start": v(273.5, -101.25) * mm, "end": v(273.5, -114.25) * mm});
            skLineSegment(sketch, "E353.MirrorCS", {"start": v(183.5, -114.25) * mm, "end": v(170.5, -114.25) * mm});
            skLineSegment(sketch, "E354.MirrorCS", {"start": v(152.5, -29.25) * mm, "end": v(165.5, -29.25) * mm});
            skLineSegment(sketch, "E355.MirrorCS", {"start": v(224.5, -42.25) * mm, "end": v(237.5, -42.25) * mm});
            skLineSegment(sketch, "E356.MirrorCS", {"start": v(188.5, -114.25) * mm, "end": v(201.5, -114.25) * mm});
            skLineSegment(sketch, "E357.MirrorCS", {"start": v(291.5, -78.25) * mm, "end": v(278.5, -78.25) * mm});
            skLineSegment(sketch, "E358.MirrorCS", {"start": v(224.5, -114.25) * mm, "end": v(237.5, -114.25) * mm});
            skLineSegment(sketch, "E359.MirrorCS", {"start": v(183.5, -83.25) * mm, "end": v(170.5, -83.25) * mm});
            skLineSegment(sketch, "E360.MirrorCS", {"start": v(273.5, -47.25) * mm, "end": v(273.5, -60.25) * mm});
            skLineSegment(sketch, "E361.MirrorCS", {"start": v(152.5, -114.25) * mm, "end": v(165.5, -114.25) * mm});
            skLineSegment(sketch, "E362.MirrorCS", {"start": v(219.5, -65.25) * mm, "end": v(219.5, -78.25) * mm});
            skLineSegment(sketch, "E363.MirrorCS", {"start": v(255.5, -47.25) * mm, "end": v(255.5, -60.25) * mm});
            skLineSegment(sketch, "E364.MirrorCS", {"start": v(242.5, -83.25) * mm, "end": v(242.5, -96.25) * mm});
            skLineSegment(sketch, "E365.MirrorCS", {"start": v(260.5, -60.25) * mm, "end": v(273.5, -60.25) * mm});
            skLineSegment(sketch, "E366.MirrorCS", {"start": v(224.5, -65.25) * mm, "end": v(237.5, -65.25) * mm});
            skLineSegment(sketch, "E367.MirrorCS", {"start": v(183.5, -101.25) * mm, "end": v(183.5, -114.25) * mm});
            skLineSegment(sketch, "E368.MirrorCS", {"start": v(260.5, -78.25) * mm, "end": v(273.5, -78.25) * mm});
            skLineSegment(sketch, "E369.MirrorCS", {"start": v(219.5, -96.25) * mm, "end": v(206.5, -96.25) * mm});
            skLineSegment(sketch, "E370.MirrorCS", {"start": v(242.5, -101.25) * mm, "end": v(242.5, -114.25) * mm});
            skLineSegment(sketch, "E371", {"start": v(294, -21.56) * mm, "end": v(294, -144.75) * mm, "construction": true});
            skLineSegment(sketch, "E372.MirrorCS", {"start": v(309.5, -83.25) * mm, "end": v(309.5, -96.25) * mm});
            skLineSegment(sketch, "E373.MirrorCS", {"start": v(314.5, -29.25) * mm, "end": v(314.5, -42.25) * mm});
            skLineSegment(sketch, "E374.MirrorCS", {"start": v(327.5, -78.25) * mm, "end": v(314.5, -78.25) * mm});
            skLineSegment(sketch, "E375.MirrorCS", {"start": v(363.5, -47.25) * mm, "end": v(350.5, -47.25) * mm});
            skLineSegment(sketch, "E376.MirrorCS", {"start": v(368.5, -101.25) * mm, "end": v(381.5, -101.25) * mm});
            skLineSegment(sketch, "E377.MirrorCS", {"start": v(368.5, -65.25) * mm, "end": v(381.5, -65.25) * mm});
            skLineSegment(sketch, "E378.MirrorCS", {"start": v(332.5, -65.25) * mm, "end": v(345.5, -65.25) * mm});
            skLineSegment(sketch, "E379.MirrorCS", {"start": v(332.5, -101.25) * mm, "end": v(345.5, -101.25) * mm});
            skLineSegment(sketch, "E380.MirrorCS", {"start": v(363.5, -132.25) * mm, "end": v(350.5, -132.25) * mm});
            skLineSegment(sketch, "E381.MirrorCS", {"start": v(296.5, -119.25) * mm, "end": v(296.5, -132.25) * mm});
            skLineSegment(sketch, "E382.MirrorCS", {"start": v(332.5, -29.25) * mm, "end": v(332.5, -42.25) * mm});
            skLineSegment(sketch, "E383.MirrorCS", {"start": v(296.5, -83.25) * mm, "end": v(296.5, -96.25) * mm});
            skLineSegment(sketch, "E384.MirrorCS", {"start": v(332.5, -83.25) * mm, "end": v(345.5, -83.25) * mm});
            skLineSegment(sketch, "E385.MirrorCS", {"start": v(296.5, -119.25) * mm, "end": v(309.5, -119.25) * mm});
            skLineSegment(sketch, "E386.MirrorCS", {"start": v(332.5, -132.25) * mm, "end": v(345.5, -132.25) * mm});
            skLineSegment(sketch, "E387.MirrorCS", {"start": v(332.5, -29.25) * mm, "end": v(345.5, -29.25) * mm});
            skLineSegment(sketch, "E388.MirrorCS", {"start": v(327.5, -83.25) * mm, "end": v(327.5, -96.25) * mm});
            skLineSegment(sketch, "E389.MirrorCS", {"start": v(363.5, -101.25) * mm, "end": v(350.5, -101.25) * mm});
            skLineSegment(sketch, "E390.MirrorCS", {"start": v(350.5, -47.25) * mm, "end": v(350.5, -60.25) * mm});
            skLineSegment(sketch, "E391.MirrorCS", {"start": v(327.5, -47.25) * mm, "end": v(327.5, -60.25) * mm});
            skLineSegment(sketch, "E392.MirrorCS", {"start": v(332.5, -119.25) * mm, "end": v(345.5, -119.25) * mm});
            skLineSegment(sketch, "E393.MirrorCS", {"start": v(363.5, -29.25) * mm, "end": v(350.5, -29.25) * mm});
            skLineSegment(sketch, "E394.MirrorCS", {"start": v(296.5, -101.25) * mm, "end": v(309.5, -101.25) * mm});
            skLineSegment(sketch, "E395.MirrorCS", {"start": v(368.5, -83.25) * mm, "end": v(381.5, -83.25) * mm});
            skLineSegment(sketch, "E396.MirrorCS", {"start": v(327.5, -96.25) * mm, "end": v(314.5, -96.25) * mm});
            skLineSegment(sketch, "E397.MirrorCS", {"start": v(314.5, -83.25) * mm, "end": v(314.5, -96.25) * mm});
            skLineSegment(sketch, "E398.MirrorCS", {"start": v(327.5, -83.25) * mm, "end": v(314.5, -83.25) * mm});
            skLineSegment(sketch, "E399.MirrorCS", {"start": v(296.5, -114.25) * mm, "end": v(309.5, -114.25) * mm});
            skLineSegment(sketch, "E400.MirrorCS", {"start": v(350.5, -29.25) * mm, "end": v(350.5, -42.25) * mm});
            skLineSegment(sketch, "E401.MirrorCS", {"start": v(381.5, -29.25) * mm, "end": v(381.5, -42.25) * mm});
            skLineSegment(sketch, "E402.MirrorCS", {"start": v(309.5, -119.25) * mm, "end": v(309.5, -132.25) * mm});
            skLineSegment(sketch, "E403.MirrorCS", {"start": v(368.5, -42.25) * mm, "end": v(381.5, -42.25) * mm});
            skLineSegment(sketch, "E404.MirrorCS", {"start": v(363.5, -29.25) * mm, "end": v(363.5, -42.25) * mm});
            skLineSegment(sketch, "E405.MirrorCS", {"start": v(314.5, -119.25) * mm, "end": v(314.5, -132.25) * mm});
            skLineSegment(sketch, "E406.MirrorCS", {"start": v(296.5, -60.25) * mm, "end": v(309.5, -60.25) * mm});
            skLineSegment(sketch, "E407.MirrorCS", {"start": v(314.5, -101.25) * mm, "end": v(314.5, -114.25) * mm});
            skLineSegment(sketch, "E408.MirrorCS", {"start": v(363.5, -78.25) * mm, "end": v(350.5, -78.25) * mm});
            skLineSegment(sketch, "E409.MirrorCS", {"start": v(350.5, -101.25) * mm, "end": v(350.5, -114.25) * mm});
            skLineSegment(sketch, "E410.MirrorCS", {"start": v(296.5, -65.25) * mm, "end": v(309.5, -65.25) * mm});
            skLineSegment(sketch, "E411.MirrorCS", {"start": v(327.5, -65.25) * mm, "end": v(314.5, -65.25) * mm});
            skLineSegment(sketch, "E412.MirrorCS", {"start": v(327.5, -101.25) * mm, "end": v(327.5, -114.25) * mm});
            skLineSegment(sketch, "E413.MirrorCS", {"start": v(327.5, -132.25) * mm, "end": v(314.5, -132.25) * mm});
            skLineSegment(sketch, "E414.MirrorCS", {"start": v(368.5, -47.25) * mm, "end": v(368.5, -60.25) * mm});
            skLineSegment(sketch, "E415.MirrorCS", {"start": v(368.5, -65.25) * mm, "end": v(368.5, -78.25) * mm});
            skLineSegment(sketch, "E416.MirrorCS", {"start": v(296.5, -65.25) * mm, "end": v(296.5, -78.25) * mm});
            skLineSegment(sketch, "E417.MirrorCS", {"start": v(327.5, -42.25) * mm, "end": v(314.5, -42.25) * mm});
            skLineSegment(sketch, "E418.MirrorCS", {"start": v(327.5, -119.25) * mm, "end": v(327.5, -132.25) * mm});
            skLineSegment(sketch, "E419.MirrorCS", {"start": v(327.5, -101.25) * mm, "end": v(314.5, -101.25) * mm});
            skLineSegment(sketch, "E420.MirrorCS", {"start": v(296.5, -101.25) * mm, "end": v(296.5, -114.25) * mm});
            skLineSegment(sketch, "E421.MirrorCS", {"start": v(350.5, -65.25) * mm, "end": v(350.5, -78.25) * mm});
            skLineSegment(sketch, "E422.MirrorCS", {"start": v(381.5, -83.25) * mm, "end": v(381.5, -96.25) * mm});
            skLineSegment(sketch, "E423.MirrorCS", {"start": v(327.5, -119.25) * mm, "end": v(314.5, -119.25) * mm});
            skLineSegment(sketch, "E424.MirrorCS", {"start": v(368.5, -119.25) * mm, "end": v(381.5, -119.25) * mm});
            skLineSegment(sketch, "E425.MirrorCS", {"start": v(332.5, -47.25) * mm, "end": v(332.5, -60.25) * mm});
            skLineSegment(sketch, "E426.MirrorCS", {"start": v(332.5, -83.25) * mm, "end": v(332.5, -96.25) * mm});
            skLineSegment(sketch, "E427.MirrorCS", {"start": v(350.5, -119.25) * mm, "end": v(350.5, -132.25) * mm});
            skLineSegment(sketch, "E428.MirrorCS", {"start": v(363.5, -47.25) * mm, "end": v(363.5, -60.25) * mm});
            skLineSegment(sketch, "E429.MirrorCS", {"start": v(368.5, -29.25) * mm, "end": v(368.5, -42.25) * mm});
            skLineSegment(sketch, "E430.MirrorCS", {"start": v(345.5, -47.25) * mm, "end": v(345.5, -60.25) * mm});
            skLineSegment(sketch, "E431.MirrorCS", {"start": v(314.5, -65.25) * mm, "end": v(314.5, -78.25) * mm});
            skLineSegment(sketch, "E432.MirrorCS", {"start": v(332.5, -60.25) * mm, "end": v(345.5, -60.25) * mm});
            skLineSegment(sketch, "E433.MirrorCS", {"start": v(363.5, -83.25) * mm, "end": v(363.5, -96.25) * mm});
            skLineSegment(sketch, "E434.MirrorCS", {"start": v(381.5, -101.25) * mm, "end": v(381.5, -114.25) * mm});
            skLineSegment(sketch, "E435.MirrorCS", {"start": v(332.5, -47.25) * mm, "end": v(345.5, -47.25) * mm});
            skLineSegment(sketch, "E436.MirrorCS", {"start": v(363.5, -96.25) * mm, "end": v(350.5, -96.25) * mm});
            skLineSegment(sketch, "E437.MirrorCS", {"start": v(332.5, -65.25) * mm, "end": v(332.5, -78.25) * mm});
            skLineSegment(sketch, "E438.MirrorCS", {"start": v(309.5, -101.25) * mm, "end": v(309.5, -114.25) * mm});
            skLineSegment(sketch, "E439.MirrorCS", {"start": v(345.5, -83.25) * mm, "end": v(345.5, -96.25) * mm});
            skLineSegment(sketch, "E440.MirrorCS", {"start": v(296.5, -47.25) * mm, "end": v(296.5, -60.25) * mm});
            skLineSegment(sketch, "E441.MirrorCS", {"start": v(368.5, -119.25) * mm, "end": v(368.5, -132.25) * mm});
            skLineSegment(sketch, "E442.MirrorCS", {"start": v(368.5, -47.25) * mm, "end": v(381.5, -47.25) * mm});
            skLineSegment(sketch, "E443.MirrorCS", {"start": v(381.5, -47.25) * mm, "end": v(381.5, -60.25) * mm});
            skLineSegment(sketch, "E444.MirrorCS", {"start": v(368.5, -60.25) * mm, "end": v(381.5, -60.25) * mm});
            skLineSegment(sketch, "E445.MirrorCS", {"start": v(332.5, -101.25) * mm, "end": v(332.5, -114.25) * mm});
            skLineSegment(sketch, "E446.MirrorCS", {"start": v(327.5, -60.25) * mm, "end": v(314.5, -60.25) * mm});
            skLineSegment(sketch, "E447.MirrorCS", {"start": v(309.5, -47.25) * mm, "end": v(309.5, -60.25) * mm});
            skLineSegment(sketch, "E448.MirrorCS", {"start": v(296.5, -96.25) * mm, "end": v(309.5, -96.25) * mm});
            skLineSegment(sketch, "E449.MirrorCS", {"start": v(363.5, -114.25) * mm, "end": v(350.5, -114.25) * mm});
            skLineSegment(sketch, "E450.MirrorCS", {"start": v(332.5, -114.25) * mm, "end": v(345.5, -114.25) * mm});
            skLineSegment(sketch, "E451.MirrorCS", {"start": v(327.5, -65.25) * mm, "end": v(327.5, -78.25) * mm});
            skLineSegment(sketch, "E452.MirrorCS", {"start": v(309.5, -29.25) * mm, "end": v(309.5, -42.25) * mm});
            skLineSegment(sketch, "E453.MirrorCS", {"start": v(345.5, -29.25) * mm, "end": v(345.5, -42.25) * mm});
            skLineSegment(sketch, "E454.MirrorCS", {"start": v(327.5, -47.25) * mm, "end": v(314.5, -47.25) * mm});
            skLineSegment(sketch, "E455.MirrorCS", {"start": v(309.5, -65.25) * mm, "end": v(309.5, -78.25) * mm});
            skLineSegment(sketch, "E456.MirrorCS", {"start": v(368.5, -114.25) * mm, "end": v(381.5, -114.25) * mm});
            skLineSegment(sketch, "E457.MirrorCS", {"start": v(296.5, -29.25) * mm, "end": v(296.5, -42.25) * mm});
            skLineSegment(sketch, "E458.MirrorCS", {"start": v(368.5, -101.25) * mm, "end": v(368.5, -114.25) * mm});
            skLineSegment(sketch, "E459.MirrorCS", {"start": v(332.5, -42.25) * mm, "end": v(345.5, -42.25) * mm});
            skLineSegment(sketch, "E460.MirrorCS", {"start": v(381.5, -119.25) * mm, "end": v(381.5, -132.25) * mm});
            skLineSegment(sketch, "E461.MirrorCS", {"start": v(363.5, -119.25) * mm, "end": v(350.5, -119.25) * mm});
            skLineSegment(sketch, "E462.MirrorCS", {"start": v(332.5, -96.25) * mm, "end": v(345.5, -96.25) * mm});
            skLineSegment(sketch, "E463.MirrorCS", {"start": v(363.5, -83.25) * mm, "end": v(350.5, -83.25) * mm});
            skLineSegment(sketch, "E464.MirrorCS", {"start": v(363.5, -42.25) * mm, "end": v(350.5, -42.25) * mm});
            skLineSegment(sketch, "E465.MirrorCS", {"start": v(314.5, -47.25) * mm, "end": v(314.5, -60.25) * mm});
            skLineSegment(sketch, "E466.MirrorCS", {"start": v(332.5, -78.25) * mm, "end": v(345.5, -78.25) * mm});
            skLineSegment(sketch, "E467.MirrorCS", {"start": v(296.5, -78.25) * mm, "end": v(309.5, -78.25) * mm});
            skLineSegment(sketch, "E468.MirrorCS", {"start": v(368.5, -29.25) * mm, "end": v(381.5, -29.25) * mm});
            skLineSegment(sketch, "E469.MirrorCS", {"start": v(332.5, -119.25) * mm, "end": v(332.5, -132.25) * mm});
            skLineSegment(sketch, "E470.MirrorCS", {"start": v(381.5, -65.25) * mm, "end": v(381.5, -78.25) * mm});
            skLineSegment(sketch, "E471.MirrorCS", {"start": v(296.5, -83.25) * mm, "end": v(309.5, -83.25) * mm});
            skLineSegment(sketch, "E472.MirrorCS", {"start": v(296.5, -29.25) * mm, "end": v(309.5, -29.25) * mm});
            skLineSegment(sketch, "E473.MirrorCS", {"start": v(327.5, -29.25) * mm, "end": v(327.5, -42.25) * mm});
            skLineSegment(sketch, "E474.MirrorCS", {"start": v(296.5, -47.25) * mm, "end": v(309.5, -47.25) * mm});
            skLineSegment(sketch, "E475.MirrorCS", {"start": v(368.5, -96.25) * mm, "end": v(381.5, -96.25) * mm});
            skLineSegment(sketch, "E476.MirrorCS", {"start": v(296.5, -42.25) * mm, "end": v(309.5, -42.25) * mm});
            skLineSegment(sketch, "E477.MirrorCS", {"start": v(368.5, -132.25) * mm, "end": v(381.5, -132.25) * mm});
            skLineSegment(sketch, "E478.MirrorCS", {"start": v(363.5, -119.25) * mm, "end": v(363.5, -132.25) * mm});
            skLineSegment(sketch, "E479.MirrorCS", {"start": v(363.5, -65.25) * mm, "end": v(350.5, -65.25) * mm});
            skLineSegment(sketch, "E480.MirrorCS", {"start": v(345.5, -65.25) * mm, "end": v(345.5, -78.25) * mm});
            skLineSegment(sketch, "E481.MirrorCS", {"start": v(363.5, -60.25) * mm, "end": v(350.5, -60.25) * mm});
            skLineSegment(sketch, "E482.MirrorCS", {"start": v(368.5, -83.25) * mm, "end": v(368.5, -96.25) * mm});
            skLineSegment(sketch, "E483.MirrorCS", {"start": v(350.5, -83.25) * mm, "end": v(350.5, -96.25) * mm});
            skLineSegment(sketch, "E484.MirrorCS", {"start": v(345.5, -119.25) * mm, "end": v(345.5, -132.25) * mm});
            skLineSegment(sketch, "E485.MirrorCS", {"start": v(296.5, -132.25) * mm, "end": v(309.5, -132.25) * mm});
            skLineSegment(sketch, "E486.MirrorCS", {"start": v(368.5, -78.25) * mm, "end": v(381.5, -78.25) * mm});
            skLineSegment(sketch, "E487.MirrorCS", {"start": v(363.5, -101.25) * mm, "end": v(363.5, -114.25) * mm});
            skLineSegment(sketch, "E488.MirrorCS", {"start": v(345.5, -101.25) * mm, "end": v(345.5, -114.25) * mm});
            skLineSegment(sketch, "E489.MirrorCS", {"start": v(363.5, -65.25) * mm, "end": v(363.5, -78.25) * mm});
            skLineSegment(sketch, "E490.MirrorCS", {"start": v(327.5, -29.25) * mm, "end": v(314.5, -29.25) * mm});
            skLineSegment(sketch, "E491.MirrorCS", {"start": v(327.5, -114.25) * mm, "end": v(314.5, -114.25) * mm});
            skCircle(sketch, "E492", {"center": v(32.44, -141.9) * mm, "radius": 1.5 * mm});
            skCircle(sketch, "E493", {"center": v(141.27, -141.9) * mm, "radius": 1.5 * mm});
            skCircle(sketch, "E494", {"center": v(248.81, -141.9) * mm, "radius": 1.5 * mm});
            skCircle(sketch, "E495", {"center": v(357.84, -141.9) * mm, "radius": 1.5 * mm});
            skCircle(sketch, "E496", {"center": v(32.44, -20) * mm, "radius": 1.5 * mm});
            skCircle(sketch, "E497", {"center": v(115, -20) * mm, "radius": 1.5 * mm});
            skCircle(sketch, "E498", {"center": v(248.81, -20) * mm, "radius": 1.5 * mm});
            skCircle(sketch, "E499", {"center": v(350.5, -20) * mm, "radius": 1.5 * mm});
            skSolve(sketch);
        }
        {
            var Q0;
            Q0 = qSketchRegion(id + "F0", true);
            extrude(context, id + "F1", {"entities" : qUnion([Q0]), "depth" : 3 * mm});
        }
        {
            var Q0;
            Q0=qCreatedBy(makeId("Top.planeOp"),FACE);
            var sketch = newSketch(context, id + "F2", { "sketchPlane" : qUnion([Q0])});
            skLineSegment(sketch, "E500.bottom", {"start": v(0, 0) * mm, "end": v(390, 0) * mm});
            skLineSegment(sketch, "E500.top", {"start": v(0, -150) * mm, "end": v(390, -150) * mm});
            skLineSegment(sketch, "E500.left", {"start": v(0, 0) * mm, "end": v(0, -150) * mm});
            skLineSegment(sketch, "E500.right", {"start": v(390, 0) * mm, "end": v(390, -150) * mm});
            skCircle(sketch, "E501", {"center": v(32.44, -20) * mm, "radius": 1.5 * mm});
            skCircle(sketch, "E502", {"center": v(115, -20) * mm, "radius": 1.5 * mm});
            skCircle(sketch, "E503", {"center": v(248.81, -20) * mm, "radius": 1.5 * mm});
            skCircle(sketch, "E504", {"center": v(350.5, -20) * mm, "radius": 1.5 * mm});
            skCircle(sketch, "E505", {"center": v(32.44, -141.9) * mm, "radius": 1.5 * mm});
            skCircle(sketch, "E506", {"center": v(141.27, -141.9) * mm, "radius": 1.5 * mm});
            skCircle(sketch, "E507", {"center": v(248.81, -141.9) * mm, "radius": 1.5 * mm});
            skCircle(sketch, "E508", {"center": v(357.84, -141.9) * mm, "radius": 1.5 * mm});
            skSolve(sketch);
        }
        {
            var Q0;
            Q0 = qSketchRegion(id + "F2", true);
            extrude(context, id + "F3", {"entities" : qUnion([Q0]), "oppositeDirection" : true, "depth" : 2 * mm});
        }
    });
